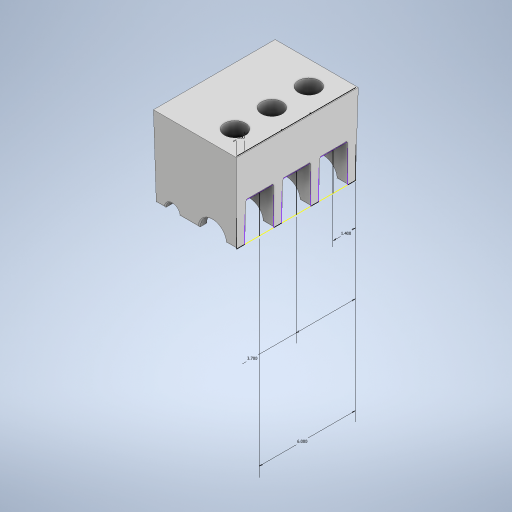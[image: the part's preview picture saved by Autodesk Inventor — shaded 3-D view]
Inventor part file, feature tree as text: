
AUTODESK INVENTOR PART (.ipt)
format: ipt  version: 2023 (Build 270158000, 158)  size: 797,696 bytes
history: native  units: in
note: dims shown in document units (in); Inventor stores cm internally (conversion verified against a paired STEP export)
features: draft x6, extrude x4, sketch x3, fillet x1
ambient origin geometry x8: Origin, YZ Plane, XZ Plane, XY Plane, X Axis, Y Axis, Z Axis, Center Point
bodies: Solid1 (feature_tree)
feature tree (14):
  extrude  "Extrusion1"  Depth=1.625in
  sketch  "Sketch2"  dims[d3=7.4in d4=0.0in d6=1.4in]
  extrude  "Extrusion2"  Depth=1.4in
  extrude  "Extrusion3"  Depth=1.4in
  extrude  "Extrusion4"  Depth=1.5in
  draft  "FaceDraft1"
  draft  "FaceDraft2"
  draft  "FaceDraft3"
  draft  "FaceDraft4"
  draft  "FaceDraft5"
  draft  "FaceDraft6"
  fillet  "Fillet1"  Radius=2.3in
  sketch  "Sketch1"  dims[d0=5.0in d2=1.625in]
  sketch  "Sketch4"  dims[d7=1.5in d10=1.4in d11=1.5in d13=2.3in d14=1.5in d15=1.4in d16=3.7in d17=6.0in d18=0.5in d20=2.528in d21=7.4in d22=0.0in d23=7.4in d24=0.0in d25=1.5in d26=0.866in d27=1.5in d28=0.0in d29=1.4in d30=5.0in d31=-0.0069in d32=0.0069in d33=0.0069in d34=0.0069in d35=0.0069in d36=0.0069in d37=0.0625in]
